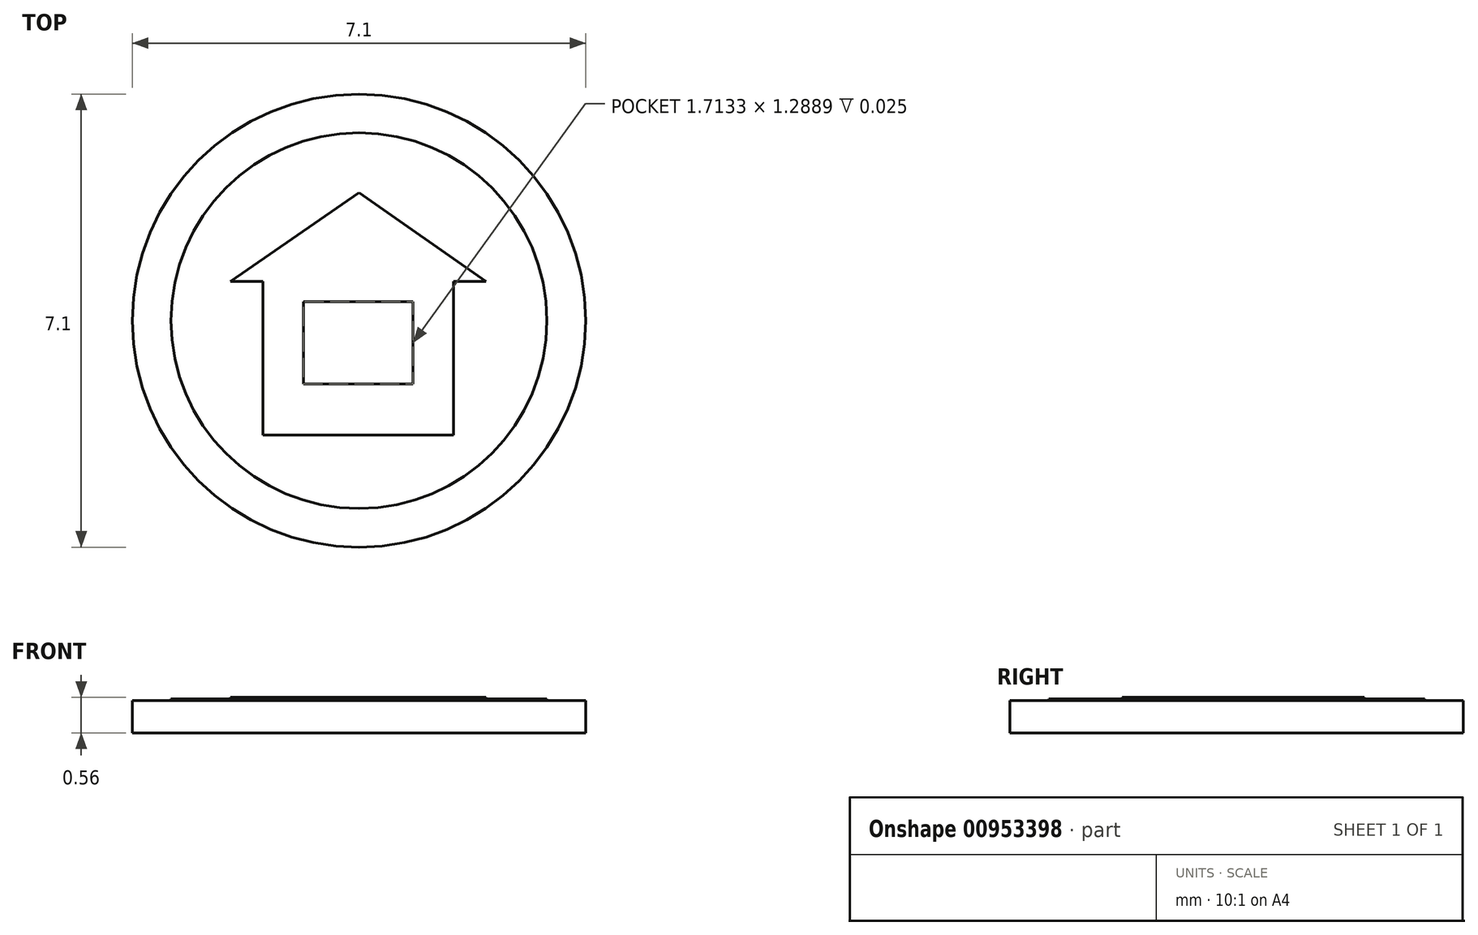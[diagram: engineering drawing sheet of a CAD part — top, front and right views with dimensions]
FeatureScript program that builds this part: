
annotation { "Feature Type Name" : "Feature", "Feature Type Description" : "" }
export const myFeature = defineFeature(function(context is Context, id is Id, definition is map)
    precondition{}
    {
        {
            var Q0;
            Q0=qCreatedBy(makeId("Top.planeOp"),FACE);
            var sketch = newSketch(context, id + "F0", { "sketchPlane" : qUnion([Q0])});
            skCircle(sketch, "E0", {"center": v(0, 0) * mm, "radius": 3.55 * mm});
            skSolve(sketch);
        }
        {
            var Q0;
            Q0=qSketchRegion(id+"F0",true);
            extrude(context, id + "F1", {"entities" : qUnion([Q0]), "depth" : 0.5 * mm, "offsetDistance" : 25.4 * mm});
        }
        {
            var Q0;
            Q0=makeQuery(id+"F1.opExtrude","CAP_FACE",FACE,{"disambiguationData":[OSD([sQuery(id+"F0.wireOp",EDGE,"E0")])],"isStart":false});
            var sketch = newSketch(context, id + "F2", { "sketchPlane" : qUnion([Q0])});
            skCircle(sketch, "E1", {"center": v(0, 0) * mm, "radius": 2.94 * mm});
            skSolve(sketch);
        }
        {
            var Q0;
            Q0=qSketchRegion(id+"F2",true);
            extrude(context, id + "F3", {"entities" : qUnion([Q0]), "operationType" : NewBodyOperationType.ADD, "depth" : 0.03 * mm, "offsetDistance" : 25.4 * mm});
        }
        {
            var Q0;
            Q0=makeQuery(id+"F3.opExtrude","CAP_FACE",FACE,{"disambiguationData":[OSD([sQuery(id+"F2.wireOp",EDGE,"E1")])],"isStart":false});
            var sketch = newSketch(context, id + "F4", { "sketchPlane" : qUnion([Q0])});
            skLineSegment(sketch, "E2", {"start": v(1.48, -1.8) * mm, "end": v(-1.5, -1.8) * mm});
            skLineSegment(sketch, "E3", {"start": v(-1.5, -1.8) * mm, "end": v(-1.5, 0.61) * mm});
            skLineSegment(sketch, "E4", {"start": v(-1.5, 0.61) * mm, "end": v(-2.01, 0.61) * mm});
            skLineSegment(sketch, "E5", {"start": v(-2.01, 0.61) * mm, "end": v(0, 2) * mm});
            skLineSegment(sketch, "E6", {"start": v(0, 2) * mm, "end": v(1.99, 0.61) * mm});
            skLineSegment(sketch, "E7", {"start": v(1.99, 0.61) * mm, "end": v(1.48, 0.61) * mm});
            skLineSegment(sketch, "E8", {"start": v(1.48, 0.61) * mm, "end": v(1.48, -1.8) * mm});
            skLineSegment(sketch, "E9", {"start": v(0.85, 0.3) * mm, "end": v(0.85, -1) * mm});
            skLineSegment(sketch, "E10", {"start": v(0.85, -1) * mm, "end": v(-0.87, -1) * mm});
            skLineSegment(sketch, "E11", {"start": v(-0.87, -1) * mm, "end": v(-0.87, 0.3) * mm});
            skLineSegment(sketch, "E12", {"start": v(-0.87, 0.3) * mm, "end": v(0.85, 0.3) * mm});
            skSolve(sketch);
        }
        {
            var Q0;
            Q0=qSketchRegion(id+"F4",true);
            extrude(context, id + "F5", {"entities" : qUnion([Q0]), "operationType" : NewBodyOperationType.ADD, "depth" : 0.03 * mm, "offsetDistance" : 25.4 * mm});
        }
    });
